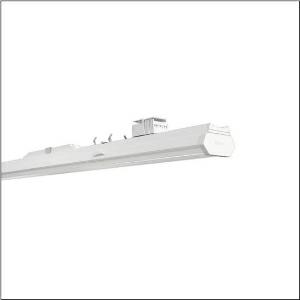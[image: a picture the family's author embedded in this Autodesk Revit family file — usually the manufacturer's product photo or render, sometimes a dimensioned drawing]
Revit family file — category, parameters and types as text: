
# Revit family: licross_r__11_protected_mo_51tp12dn595gd_f591
name_source: partatom
category: Lighting Fixtures
units: mm (PartAtom-declared; Revit-internal decimal feet)

## family parameters
Cut with Voids When Loaded = No
Host = Face
Light Source = No
Part Type = Normal
Room Calculation Point = No
Round Connector Dimension = Use Diameter
Shared = No

## types (1)
- --- (1 x LED, 1580 lm, 9.9 W, 5000K)
    Apparent Load = 10 VA
    CIE Flux Codes = 73 92 98 99 100
    Color Rendering = 80
    Color Temperature = 5000K
    Default Elevation = 1800 mm
    Description = Licross® 11 Protected MO, luminaire insert, of sheet steel, galvanised, coil coated, white, length: 1.500mm, width: 90mm, height: 101mm, LED rated luminous flux: 9.820lm, light colour: 850, control gear: DALI 2 (for two DALI lines), with plug, 6-pole, with phase selection, mains connection: 220..240V, AC/DC, 0/50..60Hz, rated input power: 57W, halogen-free wiring, for central battery installations according to DIN EN 60598-2-22, for emergency light function, without changeover relay, primary optical cover: cover, of PMMA, light emission: direct distribution, primary light characteristic: symmetric, protection rating (complete): IP64, insulation class (complete): insulation class I (protective earthing), certification: CE, ENEC, VDE, UKCA, protection symbol: D if used in an environment without relevant dust loads with corresponding accessories, impact resistance: IK06, permissible ambient temperature for indoor applications: -25..+35°C, standard: EN 60598-2-22, corresponds to IFS (International Featured Standards) requirements for safety and quality in the food industry, reducing of maximum allowable ambient temperature of 5°C with ceiling mounting, LABS conformity tested according to VDMA 24364:2018-05, packaging unit: 1 piece
    Height = 92 mm
    Lamp = 1 x LED
    Lamp Light Flux = 1580 lm
    Lamp Power = 9.9 W
    Lamp count = 1
    Length = 1500 mm
    Luminous efficacy = 160 lm/W
    Manufacturer = Siteco
    ModVariant = No
    Model = 51TP12DN595GD
    Mounting Place = Ceiling
    Mounting Type = Pendant
    Number of Poles = 1
    OnlyDefault = Yes
    Power Factor = 1
    Product Name = Licross® 11 Protected MO
    Product group = luminaire insert
    ProductGroupID = 902
    Protection Class = Protection class I
    Protection Degree = IP 64
    RLX_Detail_Level = 1
    RLX_Emergency_Light_Flux = 0 lm
    RLX_Emergency_Type = 0
    RLX_Emergency_Type_DB = No
    RlxData = <blob elided: 24869 chars, md5=673c90a6>
    Socket = socket
    Standby Power = 0 W
    System Light Flux = 1580 lm
    System Power = 10 W
    Type Comments = : DC mode (central or group accumulator) initial emergency light level
    Type Image = l_1256148.jpg
    URL = http://relux.com
    VarID = @adj_022616
    Voltage = 0 V
    Weight = 0.00 kg
    Width = 88 mm

## geometry (parser evidence)
native form markers: Blend x4, Sweep x9
no freeform markers — native parametric forms only
